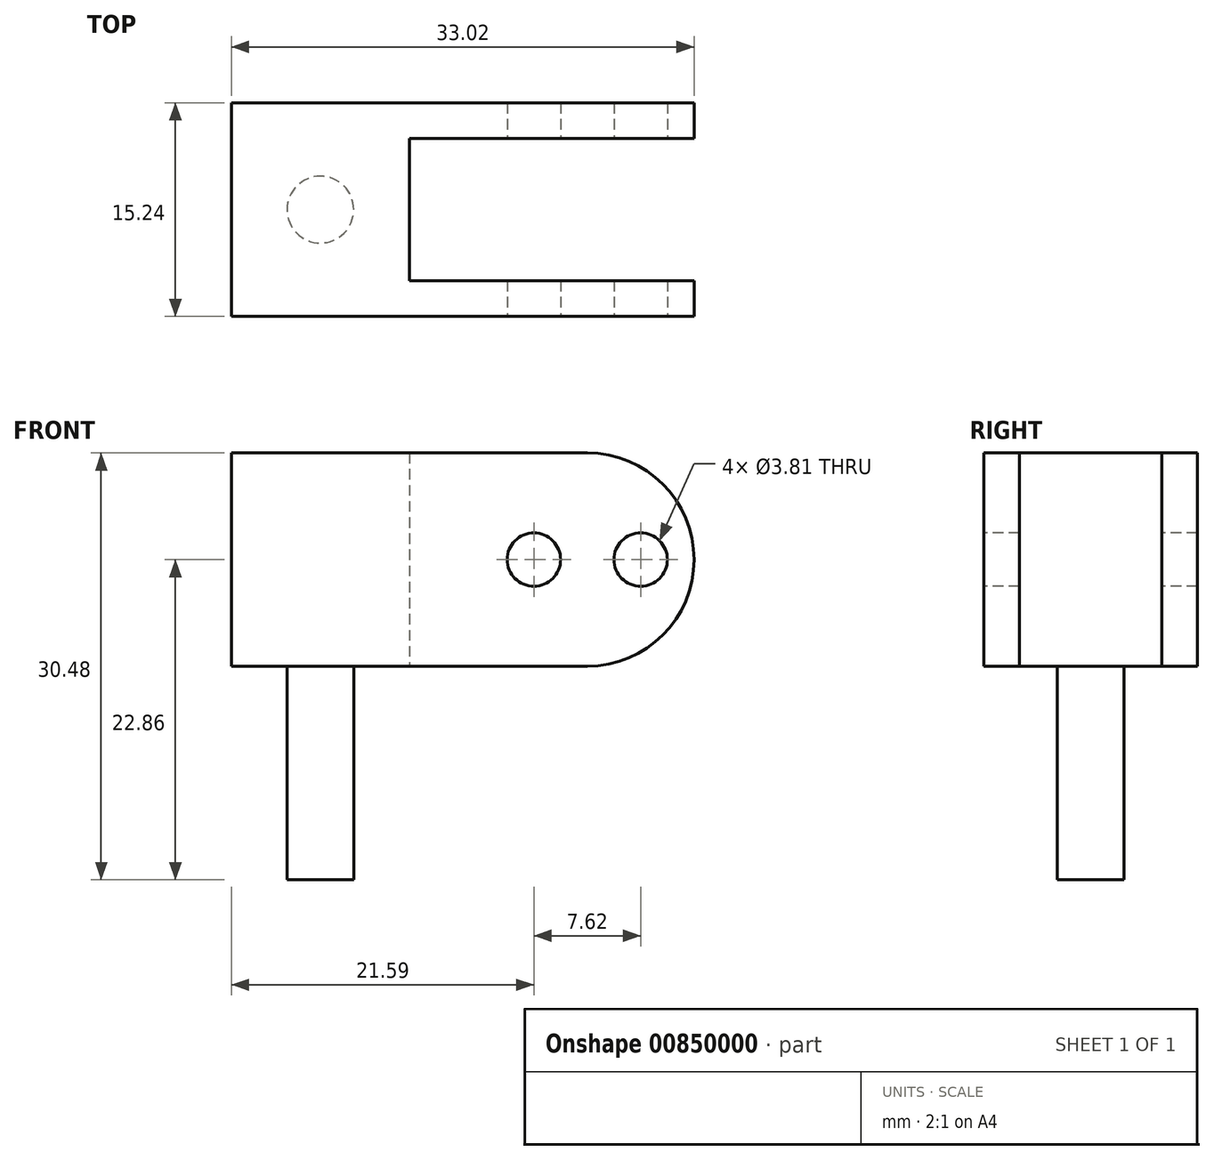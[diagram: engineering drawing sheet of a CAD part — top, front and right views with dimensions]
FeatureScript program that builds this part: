
annotation { "Feature Type Name" : "Feature", "Feature Type Description" : "" }
export const myFeature = defineFeature(function(context is Context, id is Id, definition is map)
    precondition{}
    {
        {
            var Q0;
            Q0=qCreatedBy(makeId("Top.planeOp"),FACE);
            var sketch = newSketch(context, id + "F0", { "sketchPlane" : qUnion([Q0])});
            skLineSegment(sketch, "E0.bottom", {"start": v(6.35, 7.62) * mm, "end": v(-6.35, 7.62) * mm});
            skLineSegment(sketch, "E0.top", {"start": v(6.35, -7.62) * mm, "end": v(-6.35, -7.62) * mm});
            skLineSegment(sketch, "E0.left", {"start": v(6.35, 7.62) * mm, "end": v(6.35, -7.62) * mm});
            skLineSegment(sketch, "E0.right", {"start": v(-6.35, 7.62) * mm, "end": v(-6.35, -7.62) * mm});
            skPoint(sketch, "E0.middle", {"position": v(0, 0) * mm});
            skSolve(sketch);
        }
        {
            var Q0;
            Q0 = qSketchRegion(id + "F0", true);
            extrude(context, id + "F1", {"entities" : qUnion([Q0]), "depth" : 15.24 * mm, "offsetDistance" : 25.4 * mm});
        }
        {
            var Q0;
            Q0=makeQuery(id+"F1.opExtrude","CAP_FACE",FACE,{"disambiguationData":[OSD([sQuery(id+"F0.wireOp",EDGE,"E0.bottom"),sQuery(id+"F0.wireOp",EDGE,"E0.top"),sQuery(id+"F0.wireOp",EDGE,"E0.left"),sQuery(id+"F0.wireOp",EDGE,"E0.right")])],"isStart":true});
            var sketch = newSketch(context, id + "F2", { "sketchPlane" : qUnion([Q0])});
            skCircle(sketch, "E1", {"center": v(0, 0) * mm, "radius": 2.38 * mm});
            skSolve(sketch);
        }
        {
            var Q0;
            Q0 = qSketchRegion(id + "F2", true);
            extrude(context, id + "F3", {"entities" : qUnion([Q0]), "operationType" : NewBodyOperationType.ADD, "depth" : 15.24 * mm, "offsetDistance" : 25.4 * mm});
        }
        {
            var Q0;
            Q0=makeQuery(id+"F1.opExtrude","SWEPT_FACE",FACE,{"disambiguationData":[OSD([sQuery(id+"F0.wireOp",EDGE,"E0.top")])]});
            var sketch = newSketch(context, id + "F4", { "sketchPlane" : qUnion([Q0])});
            skLineSegment(sketch, "E2.bottom", {"start": v(6.35, 15.24) * mm, "end": v(19.05, 15.24) * mm});
            skLineSegment(sketch, "E2.top", {"start": v(6.35, 0) * mm, "end": v(19.05, 0) * mm});
            skLineSegment(sketch, "E2.left", {"start": v(6.35, 15.24) * mm, "end": v(6.35, 0) * mm});
            skLineSegment(sketch, "E2.right", {"start": v(19.05, 15.24) * mm, "end": v(19.05, 0) * mm});
            skArc(sketch, "E3", {"start": v(19.05, 0) * mm, "mid": v(26.67, 7.62) * mm, "end": v(19.05, 15.24) * mm});
            skSolve(sketch);
        }
        {
            var Q0;
            Q0=makeQuery(id+"F4.imprint","IMPRINT",FACE,{"disambiguationData":[TD([[makeQuery(id+"F4.imprint","IMPRINT",EDGE,{"derivedFrom":sQuery(id+"F4.wireOp",EDGE,"E2.bottom")}),-1.0]])]});
            var Q1;
            Q1=makeQuery(id+"F4.imprint","IMPRINT",FACE,{"disambiguationData":[TD([[makeQuery(id+"F4.imprint","IMPRINT",EDGE,{"derivedFrom":sQuery(id+"F4.wireOp",EDGE,"E2.right")}),1.0]])]});
            extrude(context, id + "F5", {"entities" : qUnion([Q0, Q1]), "operationType" : NewBodyOperationType.ADD, "oppositeDirection" : true, "depth" : 2.54 * mm, "offsetDistance" : 25.4 * mm});
        }
        {
            var Q0;
            Q0=makeQuery(id+"F1.opExtrude","SWEPT_BODY",BODY,{"disambiguationData":[OSD([sQuery(id+"F0.wireOp",EDGE,"E0.bottom"),sQuery(id+"F0.wireOp",EDGE,"E0.top"),sQuery(id+"F0.wireOp",EDGE,"E0.left"),sQuery(id+"F0.wireOp",EDGE,"E0.right")])]});
            var Q1;
            Q1=qCreatedBy(makeId("Front.planeOp"),FACE);
            mirror(context, id + "F6", {"operationType" : NewBodyOperationType.ADD, "entities" : qUnion([Q0]), "mirrorPlane" : qUnion([Q1])});
        }
        {
            var Q0;
            Q0=makeQuery(id+"F5.boolean.opBoolean","MERGE",FACE,{"derivedFrom":[makeQuery(id+"F1.opExtrude","SWEPT_FACE",FACE,{"disambiguationData":[OSD([sQuery(id+"F0.wireOp",EDGE,"E0.top")])]}),makeQuery(id+"F5.opExtrude","CAP_FACE",FACE,{"disambiguationData":[OSD([sQuery(id+"F4.wireOp",EDGE,"E2.bottom"),sQuery(id+"F4.wireOp",EDGE,"E2.top"),sQuery(id+"F4.wireOp",EDGE,"E2.left"),sQuery(id+"F4.wireOp",EDGE,"E3")])],"isStart":true})]});
            var sketch = newSketch(context, id + "F7", { "sketchPlane" : qUnion([Q0])});
            skCircle(sketch, "E4", {"center": v(15.24, 7.62) * mm, "radius": 1.9 * mm});
            skCircle(sketch, "E5", {"center": v(22.86, 7.62) * mm, "radius": 1.9 * mm});
            skSolve(sketch);
        }
        {
            var Q0;
            Q0 = qSketchRegion(id + "F7", true);
            extrude(context, id + "F8", {"entities" : qUnion([Q0]), "operationType" : NewBodyOperationType.REMOVE, "endBound" : BoundingType.THROUGH_ALL, "oppositeDirection" : true, "depth" : 25.4 * mm, "offsetDistance" : 25.4 * mm});
        }
    });
